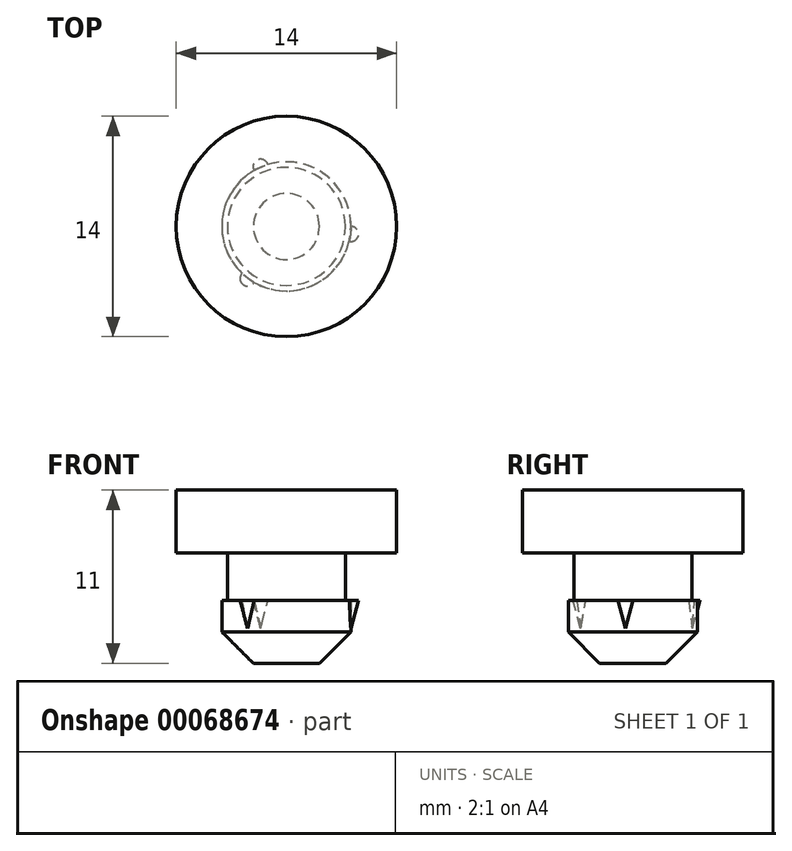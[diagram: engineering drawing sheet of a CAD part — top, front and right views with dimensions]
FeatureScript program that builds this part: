
annotation { "Feature Type Name" : "Feature", "Feature Type Description" : "" }
export const myFeature = defineFeature(function(context is Context, id is Id, definition is map)
    precondition{}
    {
        {
            var Q0;
            Q0=qCreatedBy(makeId("Top.planeOp"),FACE);
            var sketch = newSketch(context, id + "F0", { "sketchPlane" : qUnion([Q0])});
            skCircle(sketch, "E0", {"center": v(0, 0) * mm, "radius": 3.75 * mm});
            skCircle(sketch, "E1", {"center": v(0, 0) * mm, "radius": 7 * mm});
            skSolve(sketch);
        }
        {
            var Q0;
            Q0 = qSketchRegion(id + "F0", true);
            var Q1;
            Q1=makeQuery(id+"F0.imprint","IMPRINT",FACE,{"disambiguationData":[TD([[makeQuery(id+"F0.imprint","IMPRINT",EDGE,{"derivedFrom":sQuery(id+"F0.wireOp",EDGE,"2d375a36-8d4f-40c9-b453-9209e3284f9c")}),1.0]])]});
            var Q2;
            Q2=makeQuery(id+"F0.imprint","IMPRINT",FACE,{"disambiguationData":[TD([[makeQuery(id+"F0.imprint","IMPRINT",EDGE,{"derivedFrom":sQuery(id+"F0.wireOp",EDGE,"E0")}),1.0]])]});
            extrude(context, id + "F1", {"entities" : qUnion([Q0, Q1, Q2]), "depth" : 4 * mm});
        }
        {
            var Q0;
            Q0=makeQuery(id+"F0.imprint","IMPRINT",FACE,{"disambiguationData":[TD([[makeQuery(id+"F0.imprint","IMPRINT",EDGE,{"derivedFrom":sQuery(id+"F0.wireOp",EDGE,"E0")}),1.0]])]});
            extrude(context, id + "F2", {"entities" : qUnion([Q0]), "operationType" : NewBodyOperationType.ADD, "oppositeDirection" : true, "depth" : 3 * mm});
        }
        {
            var Q0;
            Q0=makeQuery(id+"F2.opExtrude","CAP_FACE",FACE,{"disambiguationData":[OSD([sQuery(id+"F0.wireOp",EDGE,"E0")])],"isStart":false});
            var sketch = newSketch(context, id + "F3", { "sketchPlane" : qUnion([Q0])});
            skCircle(sketch, "E2", {"center": v(0, 0) * mm, "radius": 4.1 * mm});
            skSolve(sketch);
        }
        {
            var Q0;
            Q0 = qSketchRegion(id + "F3", true);
            extrude(context, id + "F4", {"entities" : qUnion([Q0]), "operationType" : NewBodyOperationType.ADD, "depth" : 2 * mm});
        }
        {
            var Q0;
            Q0=makeQuery(id+"F4.opExtrude","CAP_FACE",FACE,{"disambiguationData":[OSD([sQuery(id+"F3.wireOp",EDGE,"E2")])],"isStart":false});
            extrude(context, id + "F5", {"entities" : qUnion([Q0]), "operationType" : NewBodyOperationType.ADD, "depth" : 2 * mm, "hasDraft" : true, "draftAngle" : 45 * degree, "draftPullDirection" : true});
        }
        {
            var Q0;
            Q0=makeQuery(id+"F0.imprint","IMPRINT",FACE,{"disambiguationData":[TD([[makeQuery(id+"F0.imprint","IMPRINT",EDGE,{"derivedFrom":sQuery(id+"F0.wireOp",EDGE,"E0")}),-1.0]])]});
            cPlane(context, id + "F6", {"entities" : qUnion([Q0]), "cplaneType" : CPlaneType.OFFSET, "offset" : 3 * mm, "oppositeDirection" : true, "width" : 150 * mm, "height" : 150 * mm});
        }
        {
            var Q0;
            Q0=qCreatedBy(id+"F6.planeOp",FACE);
            var sketch = newSketch(context, id + "F7", { "sketchPlane" : qUnion([Q0])});
            skCircle(sketch, "E3.0", {"center": v(0, 0) * mm, "radius": 4.1 * mm});
            skArc(sketch, "E4", {"start": v(4, -0.94) * mm, "mid": v(4.58, -0.53) * mm, "end": v(4.1, 0) * mm});
            skArc(sketch, "E5.1.0", {"start": v(-1.18, 3.93) * mm, "mid": v(-1.83, 4.23) * mm, "end": v(-2.05, 3.55) * mm});
            skArc(sketch, "E5.2.0", {"start": v(-2.81, -2.98) * mm, "mid": v(-2.75, -3.7) * mm, "end": v(-2.05, -3.55) * mm});
            skSolve(sketch);
        }
        {
            var Q0;
            {var subQ0=sQuery(id+"F7.wireOp",EDGE,"E5.1.0");Q0=makeQuery(id+"F7.imprint","IMPRINT",FACE,{"disambiguationData":[TD([[makeQuery(id+"F7.imprint","IMPRINT",EDGE,{"derivedFrom":subQ0}),1.0]])]});}
            var Q1;
            {var subQ0=sQuery(id+"F7.wireOp",EDGE,"E4");Q1=makeQuery(id+"F7.imprint","IMPRINT",FACE,{"disambiguationData":[TD([[makeQuery(id+"F7.imprint","IMPRINT",EDGE,{"derivedFrom":subQ0}),1.0]])]});}
            var Q2;
            {var subQ0=sQuery(id+"F7.wireOp",EDGE,"E5.2.0");Q2=makeQuery(id+"F7.imprint","IMPRINT",FACE,{"disambiguationData":[TD([[makeQuery(id+"F7.imprint","IMPRINT",EDGE,{"derivedFrom":subQ0}),1.0]])]});}
            extrude(context, id + "F8", {"entities" : qUnion([Q0, Q1, Q2]), "operationType" : NewBodyOperationType.ADD, "oppositeDirection" : true, "depth" : 2 * mm, "hasDraft" : true, "draftAngle" : 15 * degree, "draftPullDirection" : true});
        }
    });
